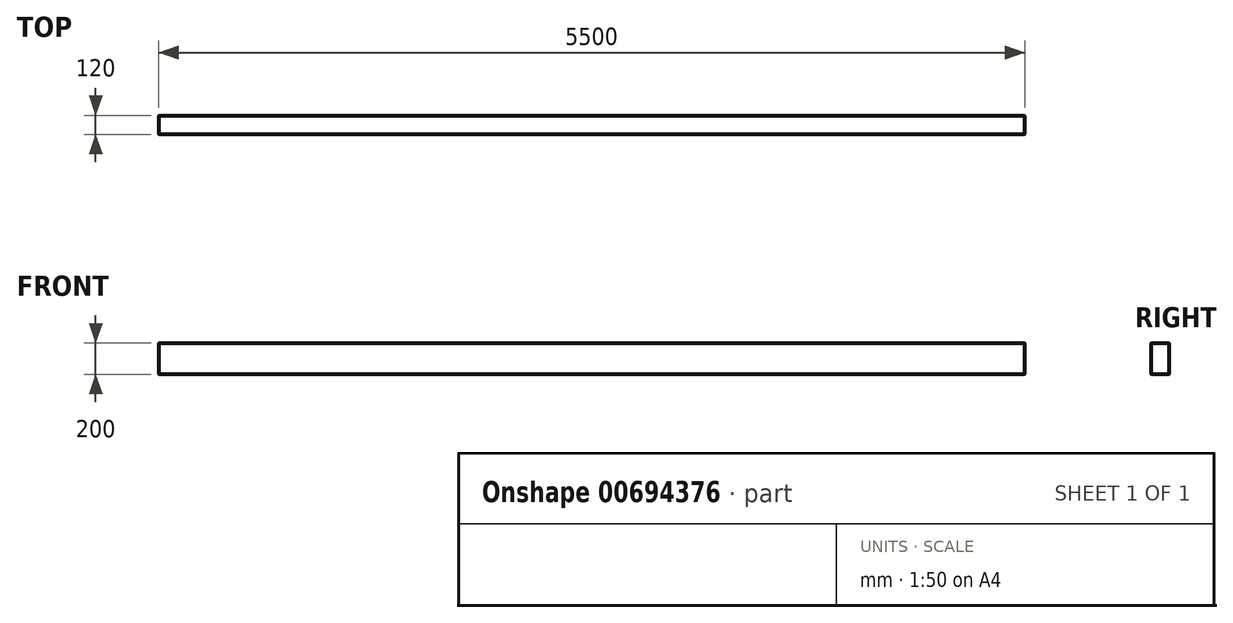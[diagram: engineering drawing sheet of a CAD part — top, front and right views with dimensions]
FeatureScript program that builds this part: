
annotation { "Feature Type Name" : "Feature", "Feature Type Description" : "" }
export const myFeature = defineFeature(function(context is Context, id is Id, definition is map)
    precondition{}
    {
        {
            var Q0;
            Q0=qCreatedBy(makeId("Top.planeOp"),FACE);
            var sketch = newSketch(context, id + "F0", { "sketchPlane" : qUnion([Q0])});
            skLineSegment(sketch, "E0.bottom", {"start": v(-700.8, -95.5) * mm, "end": v(4799.2, -95.5) * mm});
            skLineSegment(sketch, "E0.top", {"start": v(-700.8, -215.5) * mm, "end": v(4799.2, -215.5) * mm});
            skLineSegment(sketch, "E0.left", {"start": v(-700.8, -95.5) * mm, "end": v(-700.8, -215.5) * mm});
            skLineSegment(sketch, "E0.right", {"start": v(4799.2, -95.5) * mm, "end": v(4799.2, -215.5) * mm});
            skSolve(sketch);
        }
        {
            var Q0;
            Q0 = qSketchRegion(id + "F0", true);
            extrude(context, id + "F1", {"entities" : qUnion([Q0]), "depth" : 200 * mm, "offsetDistance" : 25 * mm});
        }
        {
            var Q0;
            Q0=makeQuery(id+"F1.opExtrude","SWEPT_FACE",FACE,{"disambiguationData":[OSD([sQuery(id+"F0.wireOp",EDGE,"E0.top")])]});
            var Q1;
            Q1=makeQuery(id+"F1.opExtrude","SWEPT_FACE",FACE,{"disambiguationData":[OSD([sQuery(id+"F0.wireOp",EDGE,"E0.bottom")])]});
            var Q2;
            Q2=makeQuery(id+"F1.opExtrude","SWEPT_FACE",FACE,{"disambiguationData":[OSD([sQuery(id+"F0.wireOp",EDGE,"E0.right")])]});
            var Q3;
            Q3=makeQuery(id+"F1.opExtrude","SWEPT_FACE",FACE,{"disambiguationData":[OSD([sQuery(id+"F0.wireOp",EDGE,"E0.left")])]});
            chamfer(context, id + "F2", {"entities" : qUnion([Q0, Q1, Q2, Q3]), "width" : 3 * mm, "tangentPropagation" : true});
        }
    });
